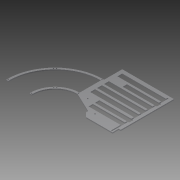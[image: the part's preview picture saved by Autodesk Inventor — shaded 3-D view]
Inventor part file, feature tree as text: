
AUTODESK INVENTOR PART (.ipt)
format: ipt  version: 2013 (Build 170138000, 138)  size: 316,928 bytes
history: native  units: in
note: dims shown in document units (in); Inventor stores cm internally (conversion verified against a paired STEP export)
features: extrude x7, sketch x7, reference x1
ambient origin geometry x8: Origin, YZ Plane, XZ Plane, XY Plane, X Axis, Y Axis, Z Axis, Center Point
feature tree (15):
  extrude  "Extrusion7"  Depth=1.0in
  extrude  "Extrusion8"  Depth=0.5in
  extrude  "Extrusion9"  Depth=5.25in
  extrude  "Extrusion10"  Depth=0.25in
  extrude  "Extrusion11"  Depth=7.625in
  extrude  "Extrusion13"  Depth=5.5in
  extrude  "Extrusion15"  Depth=12.125in
  sketch  "Sketch1"  dims[d2=0.5in d3=0.5in d10=0.5in d11=0.5in d13=0.5in d14=0.266in d15=0.266in d16=0.266in d18=0.266in d20=0.25in d21=0.266in d22=0.266in d23=0.266in d26=0.266in d30=0.266in d32=0.266in d66=1.0in]
  sketch  "Sketch7"  dims[d67=0.0in d72=0.5in]
  sketch  "Sketch8"  dims[d81=4.25in d82=5.25in]
  sketch  "Sketch9"  dims[d83=11.0in d84=0.25in]
  sketch  "Sketch10"  dims[d85=12.5in d86=7.625in]
  sketch  "Sketch13"  dims[d87=2.1762in d88=5.5in]
  sketch  "Sketch14"  dims[d89=0.25in d90=0.0in d91=12.125in d92=1.0in d93=8.0in d94=0.5in d95=2.75in d98=0.25in d99=0.0in d100=90.0deg d101=0.875in d102=0.75in d103=1.125in d104=10.5in d105=1.125in d106=0.75in d107=0.5in d108=10.5in d109=1.125in d110=1.125in d111=0.5in d112=0.5in d113=10.5in d114=0.75in d115=0.75in d116=1.0in d117=0.0in d118=11.125in d119=0.25in d120=11.5in d121=1.0in d122=0.0in d123=0.5in d124=1.375in d125=135.0deg d126=0.25in d127=0.0in d135=1.0in d136=13.25in d137=0.5in d138=1.0in d139=0.0in d146=0.25in d148=0.25in d149=0.375in d150=1.0in d151=0.0in]
  reference  "Reference4"
